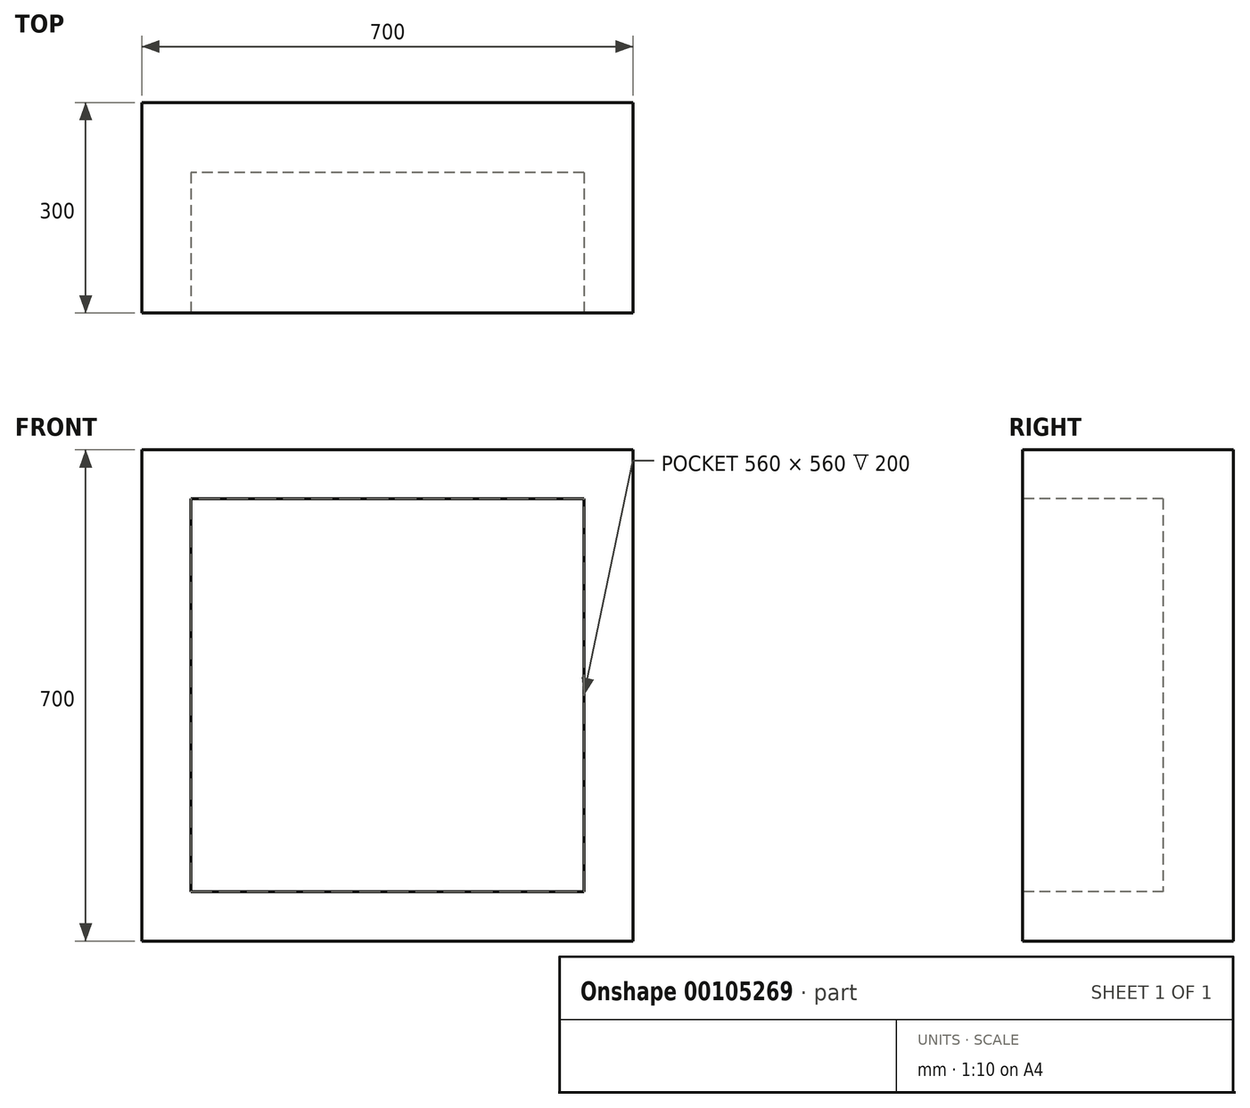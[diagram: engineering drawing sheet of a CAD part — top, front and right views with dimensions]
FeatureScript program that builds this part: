
annotation { "Feature Type Name" : "Feature", "Feature Type Description" : "" }
export const myFeature = defineFeature(function(context is Context, id is Id, definition is map)
    precondition{}
    {
        {
            var Q0;
            Q0=qCreatedBy(makeId("Front.planeOp"),FACE);
            var sketch = newSketch(context, id + "F0", { "sketchPlane" : qUnion([Q0])});
            skLineSegment(sketch, "E0.bottom", {"start": v(0, 0) * mm, "end": v(-700, 0) * mm});
            skLineSegment(sketch, "E0.top", {"start": v(0, 700) * mm, "end": v(-700, 700) * mm});
            skLineSegment(sketch, "E0.left", {"start": v(0, 0) * mm, "end": v(0, 700) * mm});
            skLineSegment(sketch, "E0.right", {"start": v(-700, 0) * mm, "end": v(-700, 700) * mm});
            skSolve(sketch);
        }
        {
            var Q0;
            Q0 = qSketchRegion(id + "F0", true);
            extrude(context, id + "F1", {"entities" : qUnion([Q0]), "depth" : 300 * mm});
        }
        {
            var Q0;
            Q0=makeQuery(id+"F1.opExtrude","CAP_FACE",FACE,{"disambiguationData":[OSD([sQuery(id+"F0.wireOp",EDGE,"E0.bottom"),sQuery(id+"F0.wireOp",EDGE,"E0.top"),sQuery(id+"F0.wireOp",EDGE,"E0.left"),sQuery(id+"F0.wireOp",EDGE,"E0.right")])],"isStart":false});
            var sketch = newSketch(context, id + "F2", { "sketchPlane" : qUnion([Q0])});
            skLineSegment(sketch, "E1.bottom", {"start": v(-70, 630) * mm, "end": v(-630, 630) * mm});
            skLineSegment(sketch, "E1.top", {"start": v(-70, 70) * mm, "end": v(-630, 70) * mm});
            skLineSegment(sketch, "E1.left", {"start": v(-70, 630) * mm, "end": v(-70, 70) * mm});
            skLineSegment(sketch, "E1.right", {"start": v(-630, 630) * mm, "end": v(-630, 70) * mm});
            skLineSegment(sketch, "E2", {"start": v(-630, 70) * mm, "end": v(-700, 70) * mm, "construction": true});
            skLineSegment(sketch, "E3", {"start": v(-70, 70) * mm, "end": v(0, 70) * mm, "construction": true});
            skLineSegment(sketch, "E4", {"start": v(-630, 630) * mm, "end": v(-630, 700) * mm, "construction": true});
            skLineSegment(sketch, "E5", {"start": v(-630, 70) * mm, "end": v(-630, 0) * mm, "construction": true});
            skSolve(sketch);
        }
        {
            var Q0;
            Q0 = qSketchRegion(id + "F2", true);
            extrude(context, id + "F3", {"entities" : qUnion([Q0]), "operationType" : NewBodyOperationType.REMOVE, "oppositeDirection" : true, "depth" : 200 * mm});
        }
    });
